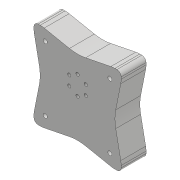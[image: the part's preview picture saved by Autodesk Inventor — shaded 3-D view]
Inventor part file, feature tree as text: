
AUTODESK INVENTOR PART (.ipt)
format: ipt  version: 2018 (Build 220112000, 112)  size: 1,816,064 bytes
history: native  units: mm
features: sketch x42, projected_geometry x36, extrude x34, fillet x9, hole x6, chamfer x5, other x2, pattern_circular x2, mirror x1, revolve x1, shell x1, plane x1, loft x1
ambient origin geometry x8: Origin, YZ Plane, XZ Plane, XY Plane, X Axis, Y Axis, Z Axis, Center Point
bodies: Solid1 (feature_tree), Solid2 (feature_tree)
feature tree (141):
  extrude  "Extrusion1"  Depth=45.0mm
  extrude  "Extrusion2"  Depth=2.25mm
  hole  "Hole1"  [1 undecoded]
  hole  "Hole2"  [1 undecoded]
  fillet  "Fillet1"  Radius=14.0mm
  extrude  "Extrusion3"  Depth=18.5mm
  extrude  "Extrusion4"  Depth=10.0mm
  extrude  "Extrusion5"  Depth=2.195mm
  extrude  "Extrusion6"  Depth=20.5mm
  hole  "Hole3"  [1 undecoded]
  extrude  "Extrusion7"  Depth=0.5mm
  extrude  "Extrusion8"  Depth=5.0mm TaperAngle=0.0deg
  extrude  "Extrusion9"  Depth=10.0mm
  extrude  "Extrusion10"  Depth=10.0mm
  extrude  "Extrusion11"  Depth=14.5mm
  extrude  "Extrusion12"  Depth=14.5mm
  extrude  "Extrusion13"  Depth=5.0mm
  extrude  "Extrusion14"  Depth=2.25mm
  extrude  "Extrusion15"  Depth=5.0mm
  extrude  "Extrusion16"  Depth=9.0mm
  extrude  "Extrusion17"  Depth=4.0mm
  chamfer  "Chamfer1"  Distance=1.0mm
  fillet  "Fillet7"  Radius=20.7mm
  fillet  "Fillet8"  Radius=32.0mm
  mirror  "Mirror1"
  extrude  "Extrusion18"  Depth=1.0mm TaperAngle=0.0deg
  extrude  "Extrusion19"  Depth=8.0mm
  extrude  "Extrusion20"  Depth=0.2mm TaperAngle=0.0deg
  extrude  "Extrusion21"  Depth=0.5mm TaperAngle=0.0deg
  extrude  "Extrusion22"  Depth=3.0mm TaperAngle=0.0deg
  extrude  "Extrusion23"  Depth=0.2mm TaperAngle=0.0deg
  extrude  "Extrusion24"  Depth=2.5mm TaperAngle=45.0deg
  sketch  "Sketch35"  dims[d91=8.0mm d92=0.0mm d93=3.0mm d94=0.0mm]
  other  "Work Axis1"
  revolve  "Revolution1"  [1 undecoded]
  extrude  "Extrusion25"  Depth=4.0mm TaperAngle=0.0deg
  extrude  "Extrusion26"  Depth=19.2mm TaperAngle=0.0deg
  shell  "Shell1"  Thickness=52.1mm
  extrude  "Extrusion27"  Depth=9.0mm
  extrude  "Extrusion28"  Depth=25.0mm
  chamfer  "Chamfer4"  Distance=6.9mm
  chamfer  "Chamfer5"  Distance=2.5mm
  extrude  "Extrusion29"  TaperAngle=90.0deg  [1 undecoded]
  pattern_circular  "Circular Pattern1"  [2 undecoded]
  fillet  "Fillet11"  Radius=5.0mm
  fillet  "Fillet12"  Radius=12.8mm
  fillet  "Fillet13"  Radius=12.8mm
  fillet  "Fillet14"  Radius=12.8mm
  chamfer  "Chamfer6"  Distance=12.8mm
  hole  "Hole6"  [1 undecoded]
  extrude  "Extrusion30"  Depth=25.0mm
  fillet  "Fillet15"  Radius=20.0mm
  extrude  "Extrusion31"  Depth=25.0mm
  plane  "Work Plane1"
  loft  "Loft1"
  hole  "Hole8"  [1 undecoded]
  extrude  "Extrusion35"  Depth=25.0mm TaperAngle=0.0deg
  chamfer  "Chamfer7"  Distance=40.0mm
  fillet  "Fillet20"  Radius=5.1mm
  extrude  "Extrusion36"  Depth=25.0mm TaperAngle=45.0deg
  extrude  "Extrusion37"  Depth=10.0mm
  hole  "Hole9"  [1 undecoded]
  pattern_circular  "Circular Pattern2"  Count=4  [1 undecoded]
  sketch  "Sketch1"  dims[d0=24.5mm d1=45.0mm]
  sketch  "Sketch2"  dims[d2=1.95mm d3=0.0mm d4=2.25mm]
  projected_geometry  "Projected Loop1"
  sketch  "Sketch3"  dims[d5=20.0mm d6=2.25mm]
  projected_geometry  "Projected Loop2"
  sketch  "Sketch4"  dims[d7=5.25mm d8=5.25mm d9=14.0mm]
  projected_geometry  "Projected Loop3"
  sketch  "Sketch5"  dims[d10=5.25mm d11=18.5mm]
  projected_geometry  "Projected Loop4"
  sketch  "Sketch6"  dims[d12=10.0mm d13=0.0mm d14=20.5mm]
  projected_geometry  "Projected Loop5"
  sketch  "Sketch7"  dims[d15=2.0mm d16=2.195mm]
  projected_geometry  "Projected Loop6"
  sketch  "Sketch8"  dims[d17=2.0mm]
  projected_geometry  "Projected Loop7"
  sketch  "Sketch9"  dims[d18=2.4mm d19=6.0mm d20=4.4mm d21=2.0mm d22=90.0deg d23=8.0mm d24=20.594885mm d25=20.5mm]
  projected_geometry  "Projected Loop8"
  projected_geometry  "Projected Loop9"
  sketch  "Sketch10"  dims[d26=26.65mm d27=2.0mm]
  projected_geometry  "Projected Loop10"
  projected_geometry  "Projected Loop11"
  sketch  "Sketch11"  dims[d28=2.0mm]
  projected_geometry  "Projected Loop12"
  sketch  "Sketch12"  dims[d29=2.4mm d30=6.0mm d31=4.4mm d32=2.0mm d33=90.0deg d34=8.0mm d35=20.594885mm d36=0.5mm]
  sketch  "Sketch13"  dims[d37=18.0mm d38=5.0mm d39=0.0mm]
  sketch  "Sketch14"  dims[d41=10.0mm d42=0.0mm d43=24.5mm]
  projected_geometry  "Projected Loop13"
  sketch  "Sketch15"  dims[d44=1.15mm d45=0.0mm d46=10.0mm]
  sketch  "Sketch16"  dims[d47=21.0mm d48=14.5mm]
  projected_geometry  "Projected Loop14"
  sketch  "Sketch17"  dims[d49=20.0mm d50=14.5mm]
  projected_geometry  "Projected Loop15"
  sketch  "Sketch18"  dims[d51=24.5mm d52=5.0mm]
  projected_geometry  "Projected Loop16"
  sketch  "Sketch19"  dims[d53=5.0mm d54=2.25mm]
  projected_geometry  "Projected Loop17"
  sketch  "Sketch20"  dims[d55=2.25mm d56=5.0mm]
  projected_geometry  "Projected Loop18"
  sketch  "Sketch22"  dims[d57=5.0mm d58=9.0mm]
  sketch  "Sketch25"  dims[d59=14.75mm d60=4.0mm d61=1.0mm d62=0.0mm d63=20.7mm]
  sketch  "Sketch27"  dims[d64=2.4mm d65=6.0mm d66=4.4mm d67=2.0mm d68=90.0deg d69=8.0mm d70=20.594885mm d72=32.0mm]
  projected_geometry  "Projected Loop22"
  sketch  "Sketch28"  dims[d73=5.0mm d74=0.0mm d75=1.0mm d76=0.0mm]
  projected_geometry  "Projected Loop23"
  sketch  "Sketch29"  dims[d77=12.25mm d78=0.0mm d80=8.0mm]
  projected_geometry  "Projected Loop24"
  sketch  "Sketch30"  dims[d81=4.5mm d82=0.0mm d84=0.2mm d85=0.0mm]
  projected_geometry  "Projected Loop25"
  sketch  "Sketch33"  dims[d86=21.0mm d87=0.5mm d88=0.0mm]
  projected_geometry  "Projected Loop26"
  sketch  "Sketch36"  dims[d95=5.0mm d96=0.0mm d98=0.2mm d99=0.0mm]
  projected_geometry  "Projected Loop27"
  sketch  "Sketch37"  dims[d100=0.2mm d101=0.0mm d102=2.5mm d103=2.0mm d104=45.0deg]
  projected_geometry  "Projected Loop28"
  sketch  "Sketch38"  dims[d105=1.5mm d114=0.5mm]
  projected_geometry  "Projected Loop29"
  projected_geometry  "Projected Loop30"
  projected_geometry  "Projected Loop31"
  projected_geometry  "Projected Loop32"
  sketch  "Sketch39"  dims[d115=22.55mm d116=0.0mm d128=4.0mm d129=0.0mm]
  projected_geometry  "Projected Loop33"
  projected_geometry  "Projected Loop34"
  sketch  "Sketch40"  dims[d130=4.0mm d131=0.0mm d132=19.2mm d133=0.0mm d134=52.1mm]
  projected_geometry  "Projected Loop35"
  sketch  "Sketch41"  dims[d135=6.8mm d136=0.0mm d137=9.0mm]
  projected_geometry  "Projected Loop36"
  sketch  "Sketch42"  dims[d138=9.0mm d139=25.0mm d140=6.9mm d141=0.0mm]
  sketch  "Sketch43"  dims[d142=5.2mm]
  projected_geometry  "Projected Loop37"
  sketch  "Sketch49"  dims[d143=5.2mm]
  other  "Edges1"
  sketch  "Sketch50"  dims[d144=5.2mm]
  sketch  "Sketch51"  dims[d145=5.2mm d146=2.5mm d147=0.0mm]
  sketch  "Sketch52"  dims[d148=5.0mm d149=90.0deg]
  projected_geometry  "Projected Loop40"
  sketch  "Sketch53"  dims[d150=5.0mm]
  sketch  "Sketch54"  dims[d151=105.0mm d152=105.0mm d153=5.0mm d154=0.0mm d156=12.8mm d157=12.8mm d158=12.8mm d159=12.8mm d160=20.0mm d161=20.0mm d162=20.0mm d163=6.0mm d164=40.0mm d165=0.0mm d166=8.0mm d167=40.0mm d168=0.0mm d169=40.0mm d170=0.0mm d178=5.1mm d179=2.45mm d180=45.0deg d181=4.1mm d182=2.45mm d183=45.0deg d184=10.0mm d185=10.0mm d186=40.0mm d187=0.0mm d188=40.0mm d189=360.0deg d191=5.1mm d192=25.0mm d193=50.0mm d194=50.0mm d195=5.0mm d196=2.0mm d197=45.0deg d198=110.0mm d199=77.781746mm d200=77.781746mm d201=4.134mm d202=10.0mm d203=12.6mm d204=2.0mm d205=90.0deg d206=14.2mm d207=20.594885mm d208=11.0mm d209=11.0mm d210=11.0mm d211=11.0mm d212=45.0mm d213=0.0mm d214=1.0mm d215=2.0mm d216=0.0mm d236=45.0mm d237=150.0mm d238=0.0mm d239=90.0deg d240=0.0mm d241=90.0deg d242=4.917mm d243=60.0mm d244=4.0mm d245=2.0mm d246=90.0deg d247=17.1mm d248=20.594885mm d249=45.0mm d250=0.0mm d251=1.0mm d252=2.0mm d253=45.0deg d254=1.0mm d255=30.0mm d256=0.0mm d257=25.0mm d258=0.0mm d259=11.5mm d260=4.134mm d261=20.0mm d262=4.0mm d263=2.0mm d264=90.0deg d265=25.0mm d266=20.594885mm d267=60.0mm d268=360.0deg]
  projected_geometry  "Project Cut Edges1"
note: 11 required parameter values undecoded (feature->parameter linkage not recoverable at this tier; creation-order binding heuristic only, values carry confidence <= 0.55)